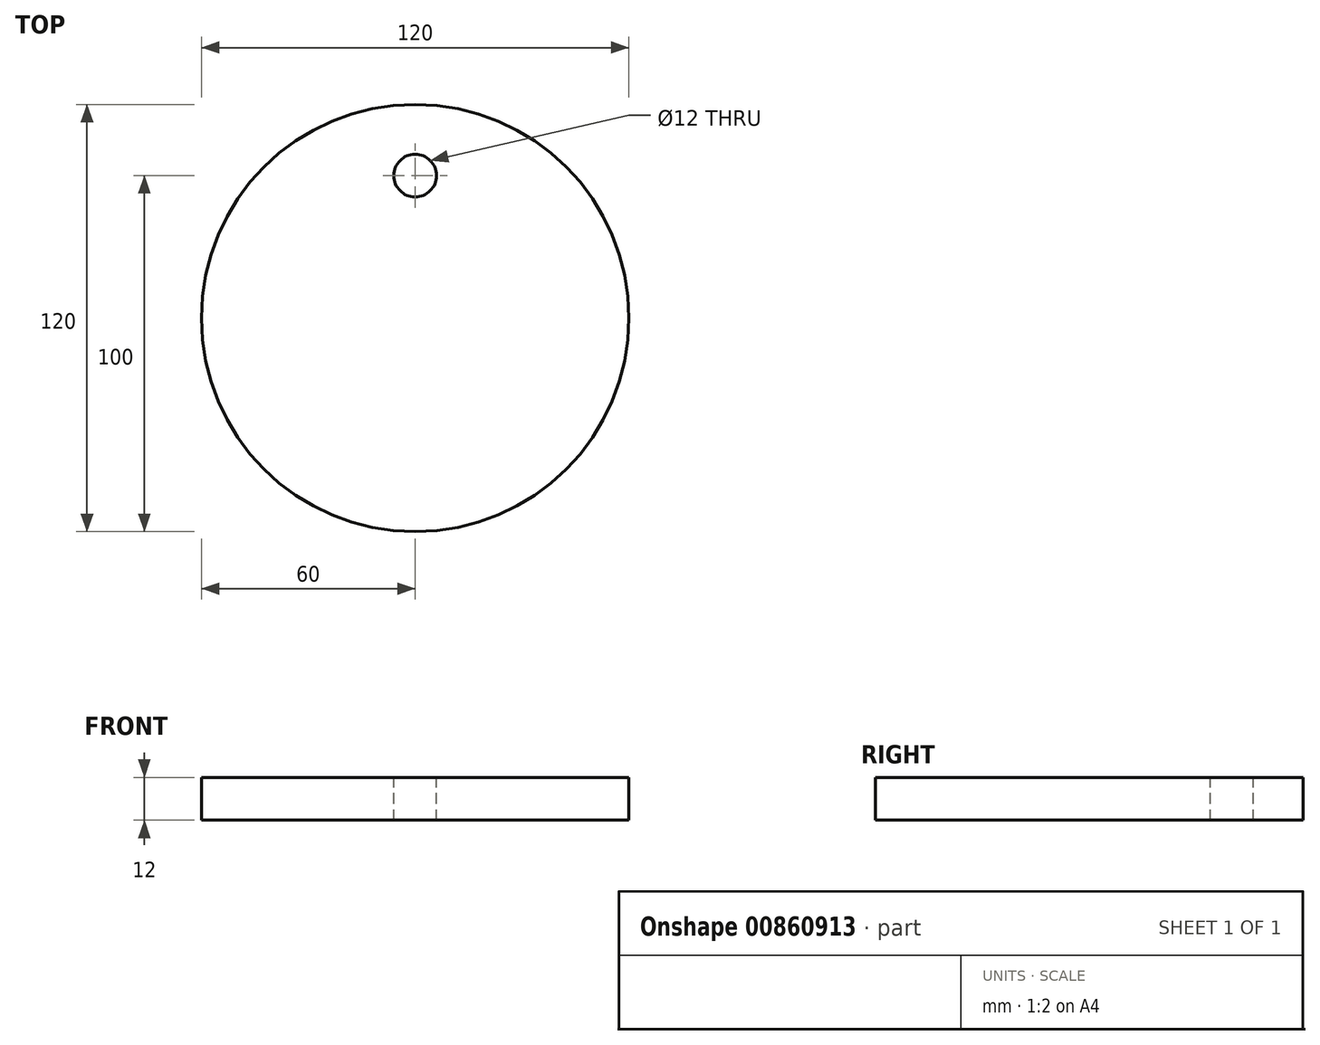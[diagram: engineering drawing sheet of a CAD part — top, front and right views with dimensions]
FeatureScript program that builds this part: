
annotation { "Feature Type Name" : "Feature", "Feature Type Description" : "" }
export const myFeature = defineFeature(function(context is Context, id is Id, definition is map)
    precondition{}
    {
        {
            assignVariable(context, id + "F0", {"name" : "BigO", "anyValue" : 120});
        }
        {
            assignVariable(context, id + "F1", {"name" : "Thickness", "anyValue" : getVariable(context, 'BigO') / 10});
        }
        {
            var Q0;
            Q0=qCreatedBy(makeId("Top.planeOp"),FACE);
            var sketch = newSketch(context, id + "F2", { "sketchPlane" : qUnion([Q0])});
            skCircle(sketch, "E0", {"center": v(0, 0) * mm, "radius": 60 * mm});
            skSolve(sketch);
        }
        {
            var Q0;
            Q0=makeQuery(id+"F2.imprint","IMPRINT",FACE,{"disambiguationData":[TD([[makeQuery(id+"F2.imprint","IMPRINT",EDGE,{"derivedFrom":sQuery(id+"F2.wireOp",EDGE,"E0")}),1.0]])]});
            extrude(context, id + "F3", {"entities" : qUnion([Q0]), "depth" : (getVariable(context, 'Thickness')) * mm, "offsetDistance" : 25 * mm});
        }
        {
            var Q0;
            Q0=makeQuery(id+"F3.opExtrude","CAP_FACE",FACE,{"disambiguationData":[OSD([sQuery(id+"F2.wireOp",EDGE,"E0")])],"isStart":false});
            var sketch = newSketch(context, id + "F4", { "sketchPlane" : qUnion([Q0])});
            skCircle(sketch, "E1", {"center": v(0, 0) * mm, "radius": 40 * mm, "construction": true});
            skCircle(sketch, "E2", {"center": v(0, 40) * mm, "radius": 6 * mm});
            skSolve(sketch);
        }
        {
            var Q0;
            Q0=makeQuery(id+"F4.imprint","IMPRINT",FACE,{"disambiguationData":[TD([[makeQuery(id+"F4.imprint","IMPRINT",EDGE,{"derivedFrom":sQuery(id+"F4.wireOp",EDGE,"E2")}),1.0]])]});
            extrude(context, id + "F5", {"entities" : qUnion([Q0]), "operationType" : NewBodyOperationType.REMOVE, "endBound" : BoundingType.THROUGH_ALL, "oppositeDirection" : true, "depth" : 25 * mm, "offsetDistance" : 25 * mm});
        }
    });
